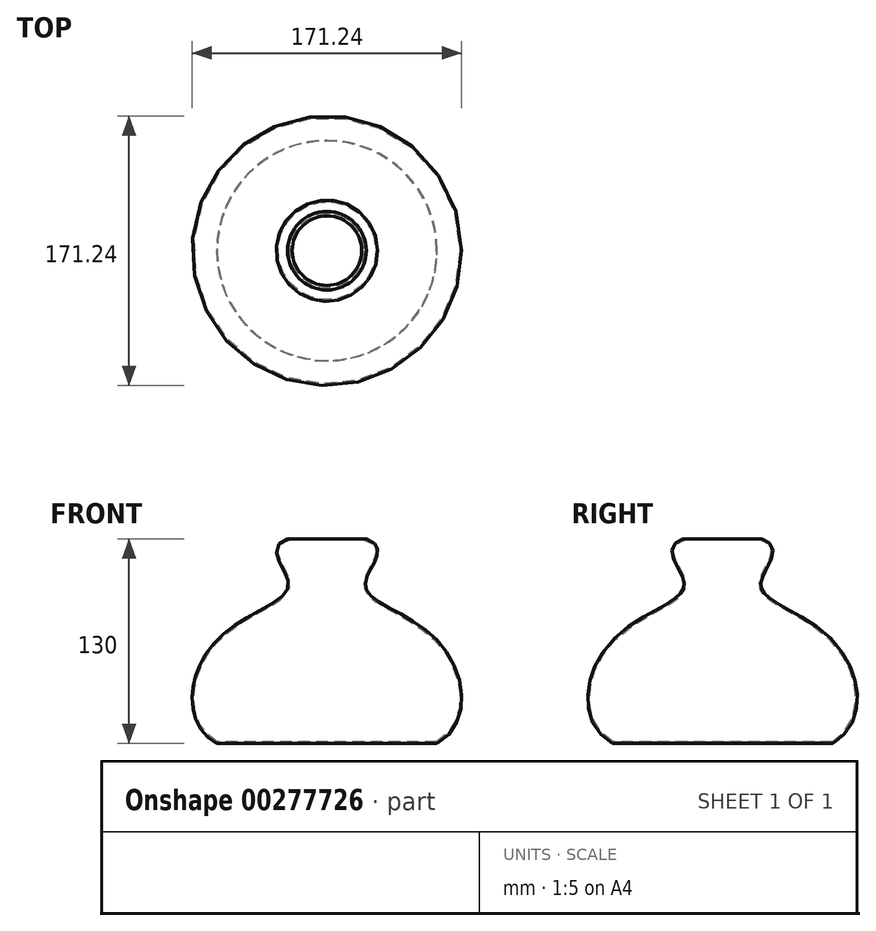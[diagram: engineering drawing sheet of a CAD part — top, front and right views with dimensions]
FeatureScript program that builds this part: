
annotation { "Feature Type Name" : "Feature", "Feature Type Description" : "" }
export const myFeature = defineFeature(function(context is Context, id is Id, definition is map)
    precondition{}
    {
        {
            var Q0;
            Q0=qCreatedBy(makeId("Front.planeOp"),FACE);
            var sketch = newSketch(context, id + "F0", { "sketchPlane" : qUnion([Q0])});
            skLineSegment(sketch, "E0", {"start": v(0, 60.73) * mm, "end": v(0, -69.27) * mm});
            skLineSegment(sketch, "E1", {"start": v(0, -69.27) * mm, "end": v(70, -69.27) * mm});
            skLineSegment(sketch, "E2", {"start": v(0, 60.73) * mm, "end": v(25, 60.73) * mm});
            skFitSpline(sketch, "E3", {"points": [v(25, 60.73) * mm, v(30.73, 47.4) * mm, v(25, 28.65) * mm, v(71.87, -5.73) * mm, v(70, -69.27) * mm], "startDerivative": vector(159.21, -57.97) * mm, "endDerivative": vector(-202.7, -117.9) * mm});
            skSolve(sketch);
        }
        {
            var Q0;
            Q0=makeQuery(id+"F0.imprint","IMPRINT",FACE,{"disambiguationData":[TD([[makeQuery(id+"F0.imprint","IMPRINT",EDGE,{"derivedFrom":sQuery(id+"F0.wireOp",EDGE,"E0")}),1.0]])]});
            var Q1;
            Q1=sQuery(id+"F0.wireOp",EDGE,"E0");
            revolve(context, id + "F1", {"entities" : qUnion([Q0]), "axis" : qUnion([Q1]), "revolveType" : RevolveType.FULL});
        }
        {
            var Q0;
            Q0=makeQuery(id+"F1.opRevolve","SWEPT_FACE",FACE,{"disambiguationData":[OSD([sQuery(id+"F0.wireOp",EDGE,"E2")])]});
            shell(context, id + "F2", {"entities" : qUnion([Q0]), "thickness" : 1 * mm});
        }
    });
